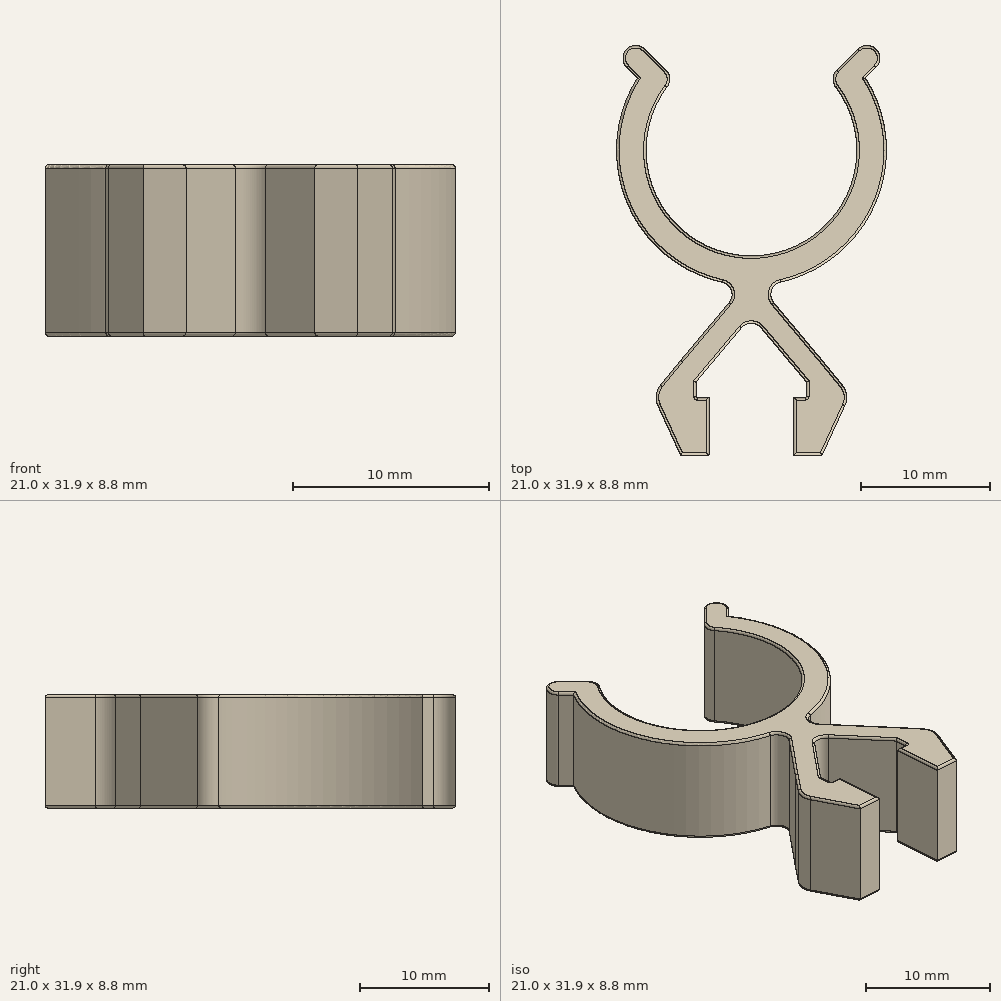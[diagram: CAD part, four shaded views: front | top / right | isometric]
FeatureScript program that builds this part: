
annotation { "Feature Type Name" : "Feature", "Feature Type Description" : "" }
export const myFeature = defineFeature(function(context is Context, id is Id, definition is map)
    precondition{}
    {
        {
            var Q0;
            Q0=qCreatedBy(makeId("Top.planeOp"),FACE);
            var sketch = newSketch(context, id + "F0", { "sketchPlane" : qUnion([Q0])});
            skArc(sketch, "E0", {"start": v(-6, 5.59) * mm, "mid": v(0, -8.2) * mm, "end": v(6, 5.59) * mm});
            skArc(sketch, "E1.0", {"start": v(-8.87, 5.63) * mm, "mid": v(-9.34, -4.8) * mm, "end": v(-0.58, -10.48) * mm});
            skLineSegment(sketch, "E2.bottom", {"start": v(6, 0) * mm, "end": v(5.5, 0) * mm, "construction": true});
            skLineSegment(sketch, "E2.top", {"start": v(6, 24.85) * mm, "end": v(-6, 24.85) * mm, "construction": true});
            skLineSegment(sketch, "E2.left", {"start": v(6, 0) * mm, "end": v(6, 24.85) * mm, "construction": true});
            skLineSegment(sketch, "E2.right", {"start": v(-6, 0) * mm, "end": v(-6, 24.85) * mm, "construction": true});
            skPoint(sketch, "E2.middle", {"position": v(0, 12.42) * mm});
            skLineSegment(sketch, "E3", {"start": v(6, 5.59) * mm, "end": v(9.04, 8.63) * mm});
            skLineSegment(sketch, "E4", {"start": v(-6, 5.59) * mm, "end": v(-9.04, 8.63) * mm});
            skLineSegment(sketch, "E5.0", {"start": v(-8.87, 5.63) * mm, "end": v(-10.3, 7.07) * mm});
            skLineSegment(sketch, "E6.0", {"start": v(8.87, 5.63) * mm, "end": v(10.3, 7.07) * mm});
            skArc(sketch, "E7.0", {"start": v(-9.04, 8.63) * mm, "mid": v(-9.7, 7.88) * mm, "end": v(-10.3, 7.07) * mm});
            skArc(sketch, "E8.trimOffspring", {"start": v(10.3, 7.07) * mm, "mid": v(9.7, 7.88) * mm, "end": v(9.04, 8.63) * mm});
            skLineSegment(sketch, "E9", {"start": v(0, -12.9) * mm, "end": v(-4.3, -18.02) * mm});
            skLineSegment(sketch, "E10", {"start": v(0, -12.9) * mm, "end": v(4.3, -18.02) * mm});
            skLineSegment(sketch, "E11.0", {"start": v(1.53, -11.61) * mm, "end": v(5.5, -16.34) * mm});
            skLineSegment(sketch, "E12.0", {"start": v(-0.58, -10.48) * mm, "end": v(-5.5, -16.34) * mm});
            skLineSegment(sketch, "E12.1", {"start": v(0.58, -10.48) * mm, "end": v(5.5, -16.34) * mm});
            skLineSegment(sketch, "E13.bottom", {"start": v(4.3, 0) * mm, "end": v(-4.3, 0) * mm, "construction": true});
            skLineSegment(sketch, "E13.top", {"start": v(4.3, -19.22) * mm, "end": v(-4.3, -19.22) * mm, "construction": true});
            skLineSegment(sketch, "E13.left", {"start": v(4.3, -18.02) * mm, "end": v(4.3, -19.22) * mm});
            skLineSegment(sketch, "E13.right", {"start": v(-4.3, -18.02) * mm, "end": v(-4.3, -19.22) * mm});
            skPoint(sketch, "E13.middle", {"position": v(0, -9.61) * mm});
            skLineSegment(sketch, "E14", {"start": v(-4.3, -19.22) * mm, "end": v(-3.3, -19.22) * mm});
            skLineSegment(sketch, "E15", {"start": v(4.3, -19.22) * mm, "end": v(3.3, -19.22) * mm});
            skArc(sketch, "E16.trimOffspring", {"start": v(0.58, -10.48) * mm, "mid": v(9.34, -4.8) * mm, "end": v(8.87, 5.63) * mm});
            skLineSegment(sketch, "E17", {"start": v(-3.3, -19.22) * mm, "end": v(-3.3, -23.72) * mm});
            skLineSegment(sketch, "E18", {"start": v(-5.5, -23.72) * mm, "end": v(-3.3, -23.72) * mm});
            skPoint(sketch, "E19.start.orphan", {"position": v(-4.4, -20.82) * mm});
            skPoint(sketch, "E20.start.orphan", {"position": v(-4.4, -23.35) * mm});
            skLineSegment(sketch, "E21", {"start": v(3.3, -19.22) * mm, "end": v(3.3, -23.72) * mm});
            skLineSegment(sketch, "E22", {"start": v(3.3, -23.72) * mm, "end": v(5.5, -23.72) * mm});
            skPoint(sketch, "E23.MirrorCS.end.orphan", {"position": v(4.4, -23.35) * mm});
            skPoint(sketch, "E23.MirrorCS.start.orphan", {"position": v(4.4, -20.82) * mm});
            skLineSegment(sketch, "E24", {"start": v(5.5, -16.34) * mm, "end": v(7.67, -19) * mm});
            skLineSegment(sketch, "E25", {"start": v(7.67, -19) * mm, "end": v(5.5, -23.72) * mm});
            skLineSegment(sketch, "E26.MirrorCS", {"start": v(-7.67, -19) * mm, "end": v(-5.5, -23.72) * mm});
            skLineSegment(sketch, "E27.MirrorCS", {"start": v(-5.5, -16.34) * mm, "end": v(-7.67, -19) * mm});
            skPoint(sketch, "E28.start.orphan", {"position": v(-5.5, -22.42) * mm});
            skPoint(sketch, "E29.MirrorCS.end.orphan", {"position": v(5.5, -23.72) * mm});
            skPoint(sketch, "E29.MirrorCS.start.orphan", {"position": v(5.5, -22.42) * mm});
            skSolve(sketch);
        }
        {
            var Q0;
            Q0 = qSketchRegion(id + "F0", true);
            extrude(context, id + "F1", {"entities" : qUnion([Q0]), "depth" : 8.8 * mm, "offsetDistance" : 25 * mm});
        }
        {
            var Q0;
            Q0=makeQuery(id+"F1.opExtrude","SWEPT_EDGE",EDGE,{"disambiguationData":[OSD([sQuery(id+"F0.wireOp",EDGE,"E0"),sQuery(id+"F0.wireOp",EDGE,"E3")])]});
            var Q1;
            Q1=makeQuery(id+"F1.opExtrude","SWEPT_EDGE",EDGE,{"disambiguationData":[OSD([sQuery(id+"F0.wireOp",EDGE,"E0"),sQuery(id+"F0.wireOp",EDGE,"E4")])]});
            var Q2;
            Q2=makeQuery(id+"F1.opExtrude","SWEPT_EDGE",EDGE,{"disambiguationData":[OSD([sQuery(id+"F0.wireOp",EDGE,"E4"),sQuery(id+"F0.wireOp",EDGE,"E7.0")])]});
            var Q3;
            Q3=makeQuery(id+"F1.opExtrude","SWEPT_EDGE",EDGE,{"disambiguationData":[OSD([sQuery(id+"F0.wireOp",EDGE,"E3"),sQuery(id+"F0.wireOp",EDGE,"E8.trimOffspring")])]});
            var Q4;
            Q4=makeQuery(id+"F1.opExtrude","SWEPT_EDGE",EDGE,{"disambiguationData":[OSD([sQuery(id+"F0.wireOp",EDGE,"E6.0"),sQuery(id+"F0.wireOp",EDGE,"E8.trimOffspring")])]});
            var Q5;
            Q5=makeQuery(id+"F1.opExtrude","SWEPT_EDGE",EDGE,{"disambiguationData":[OSD([sQuery(id+"F0.wireOp",EDGE,"E5.0"),sQuery(id+"F0.wireOp",EDGE,"E7.0")])]});
            var Q6;
            Q6=makeQuery(id+"F1.opExtrude","SWEPT_EDGE",EDGE,{"disambiguationData":[OSD([sQuery(id+"F0.wireOp",EDGE,"E12.1"),sQuery(id+"F0.wireOp",EDGE,"E16.trimOffspring")])]});
            var Q7;
            Q7=makeQuery(id+"F1.opExtrude","SWEPT_EDGE",EDGE,{"disambiguationData":[OSD([sQuery(id+"F0.wireOp",EDGE,"E1.0"),sQuery(id+"F0.wireOp",EDGE,"E12.0")])]});
            fillet(context, id + "F2", {"entities" : qUnion([Q0, Q1, Q2, Q3, Q4, Q5, Q6, Q7]), "radius" : 1 * mm, "tangentPropagation" : true, "allowEdgeOverflow" : false});
        }
        {
            var Q0;
            Q0=makeQuery(id+"F1.opExtrude","SWEPT_EDGE",EDGE,{"disambiguationData":[OSD([sQuery(id+"F0.wireOp",EDGE,"E13.right"),sQuery(id+"F0.wireOp",EDGE,"E14")])]});
            var Q1;
            Q1=makeQuery(id+"F1.opExtrude","SWEPT_EDGE",EDGE,{"disambiguationData":[OSD([sQuery(id+"F0.wireOp",EDGE,"E13.left"),sQuery(id+"F0.wireOp",EDGE,"E15")])]});
            fillet(context, id + "F3", {"entities" : qUnion([Q0, Q1]), "radius" : .1 * mm, "tangentPropagation" : true, "allowEdgeOverflow" : false});
        }
        {
            var Q0;
            Q0=makeQuery(id+"F1.opExtrude","SWEPT_EDGE",EDGE,{"disambiguationData":[OSD([sQuery(id+"F0.wireOp",EDGE,"E9"),sQuery(id+"F0.wireOp",EDGE,"E10")])]});
            fillet(context, id + "F4", {"entities" : qUnion([Q0]), "radius" : 1 * mm, "tangentPropagation" : true, "allowEdgeOverflow" : false});
        }
        {
            var Q0;
            Q0=makeQuery(id+"F1.opExtrude","SWEPT_EDGE",EDGE,{"disambiguationData":[OSD([sQuery(id+"F0.wireOp",EDGE,"4549472e-fbb2-4b83-84f1-c5aa3998a7b9.0"),sQuery(id+"F0.wireOp",EDGE,"xXLjAbvo-KHdO-mt6C-3fN5-gnB2EINuDtOB")])]});
            var Q1;
            Q1=makeQuery(id+"F1.opExtrude","SWEPT_EDGE",EDGE,{"disambiguationData":[OSD([sQuery(id+"F0.wireOp",EDGE,"61cc0a00-dde1-4ecb-828d-98507be19cde.0"),sQuery(id+"F0.wireOp",EDGE,"QX6jjFFv-lzwQ-gi6A-r10G-BnhjMFURtk5V")])]});
            var Q2;
            Q2=makeQuery(id+"F1.opExtrude","SWEPT_EDGE",EDGE,{"disambiguationData":[OSD([sQuery(id+"F0.wireOp",EDGE,"E12.1"),sQuery(id+"F0.wireOp",EDGE,"61cc0a00-dde1-4ecb-828d-98507be19cde.0")])]});
            var Q3;
            Q3=makeQuery(id+"F1.opExtrude","SWEPT_EDGE",EDGE,{"disambiguationData":[OSD([sQuery(id+"F0.wireOp",EDGE,"E12.0"),sQuery(id+"F0.wireOp",EDGE,"4549472e-fbb2-4b83-84f1-c5aa3998a7b9.0")])]});
            fillet(context, id + "F5", {"entities" : qUnion([Q0, Q1, Q2, Q3]), "radius" : .5 * mm, "tangentPropagation" : true, "allowEdgeOverflow" : false});
        }
        {
            var Q0;
            Q0=makeQuery(id+"F1.opExtrude","CAP_FACE",FACE,{"disambiguationData":[OSD([sQuery(id+"F0.wireOp",EDGE,"E0"),sQuery(id+"F0.wireOp",EDGE,"E1.0"),sQuery(id+"F0.wireOp",EDGE,"E3"),sQuery(id+"F0.wireOp",EDGE,"E4"),sQuery(id+"F0.wireOp",EDGE,"E5.0"),sQuery(id+"F0.wireOp",EDGE,"E6.0"),sQuery(id+"F0.wireOp",EDGE,"E7.0"),sQuery(id+"F0.wireOp",EDGE,"E8.trimOffspring"),sQuery(id+"F0.wireOp",EDGE,"E9"),sQuery(id+"F0.wireOp",EDGE,"E10"),sQuery(id+"F0.wireOp",EDGE,"E12.0"),sQuery(id+"F0.wireOp",EDGE,"E12.1"),sQuery(id+"F0.wireOp",EDGE,"E13.left"),sQuery(id+"F0.wireOp",EDGE,"E13.right"),sQuery(id+"F0.wireOp",EDGE,"61cc0a00-dde1-4ecb-828d-98507be19cde.0"),sQuery(id+"F0.wireOp",EDGE,"4549472e-fbb2-4b83-84f1-c5aa3998a7b9.0"),sQuery(id+"F0.wireOp",EDGE,"E14"),sQuery(id+"F0.wireOp",EDGE,"E15"),sQuery(id+"F0.wireOp",EDGE,"xXLjAbvo-KHdO-mt6C-3fN5-gnB2EINuDtOB"),sQuery(id+"F0.wireOp",EDGE,"QX6jjFFv-lzwQ-gi6A-r10G-BnhjMFURtk5V"),sQuery(id+"F0.wireOp",EDGE,"E16.trimOffspring")])],"isStart":false});
            var Q1;
            Q1=makeQuery(id+"F1.opExtrude","CAP_FACE",FACE,{"disambiguationData":[OSD([sQuery(id+"F0.wireOp",EDGE,"E0"),sQuery(id+"F0.wireOp",EDGE,"E1.0"),sQuery(id+"F0.wireOp",EDGE,"E3"),sQuery(id+"F0.wireOp",EDGE,"E4"),sQuery(id+"F0.wireOp",EDGE,"E5.0"),sQuery(id+"F0.wireOp",EDGE,"E6.0"),sQuery(id+"F0.wireOp",EDGE,"E7.0"),sQuery(id+"F0.wireOp",EDGE,"E8.trimOffspring"),sQuery(id+"F0.wireOp",EDGE,"E9"),sQuery(id+"F0.wireOp",EDGE,"E10"),sQuery(id+"F0.wireOp",EDGE,"E12.0"),sQuery(id+"F0.wireOp",EDGE,"E12.1"),sQuery(id+"F0.wireOp",EDGE,"E13.left"),sQuery(id+"F0.wireOp",EDGE,"E13.right"),sQuery(id+"F0.wireOp",EDGE,"61cc0a00-dde1-4ecb-828d-98507be19cde.0"),sQuery(id+"F0.wireOp",EDGE,"4549472e-fbb2-4b83-84f1-c5aa3998a7b9.0"),sQuery(id+"F0.wireOp",EDGE,"E14"),sQuery(id+"F0.wireOp",EDGE,"E15"),sQuery(id+"F0.wireOp",EDGE,"xXLjAbvo-KHdO-mt6C-3fN5-gnB2EINuDtOB"),sQuery(id+"F0.wireOp",EDGE,"QX6jjFFv-lzwQ-gi6A-r10G-BnhjMFURtk5V"),sQuery(id+"F0.wireOp",EDGE,"E16.trimOffspring")])],"isStart":true});
            fillet(context, id + "F6", {"entities" : qUnion([Q0, Q1]), "radius" : .2 * mm, "tangentPropagation" : true, "allowEdgeOverflow" : false});
        }
        {
            var Q0;
            Q0=makeQuery(id+"F1.opExtrude","SWEPT_EDGE",EDGE,{"disambiguationData":[OSD([sQuery(id+"F0.wireOp",EDGE,"E26.MirrorCS"),sQuery(id+"F0.wireOp",EDGE,"E27.MirrorCS")])]});
            var Q1;
            Q1=makeQuery(id+"F1.opExtrude","SWEPT_EDGE",EDGE,{"disambiguationData":[OSD([sQuery(id+"F0.wireOp",EDGE,"E24"),sQuery(id+"F0.wireOp",EDGE,"E25")])]});
            fillet(context, id + "F7", {"entities" : qUnion([Q0, Q1]), "radius" : 1.5 * mm, "tangentPropagation" : true, "allowEdgeOverflow" : false});
        }
    });
